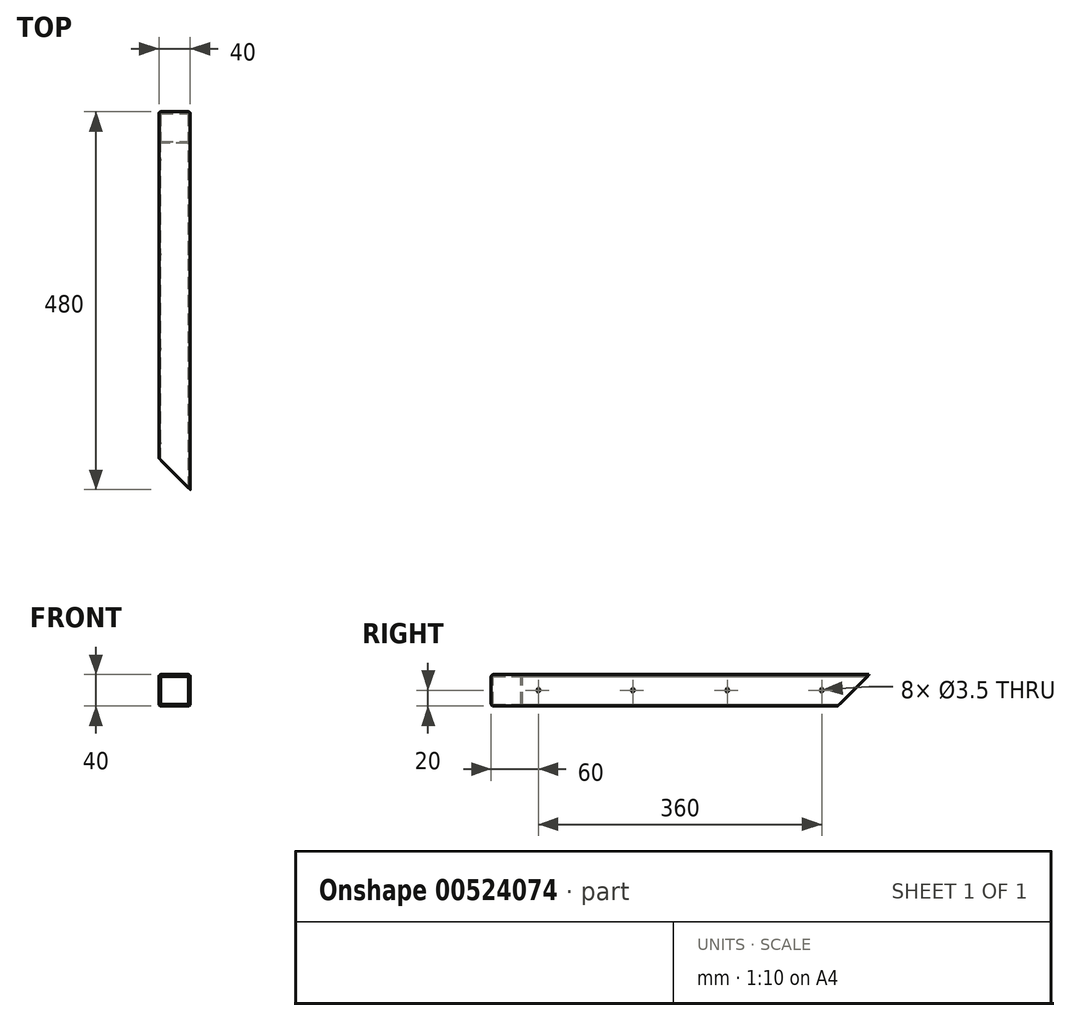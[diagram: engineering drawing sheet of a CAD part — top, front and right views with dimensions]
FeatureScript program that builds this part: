
annotation { "Feature Type Name" : "Feature", "Feature Type Description" : "" }
export const myFeature = defineFeature(function(context is Context, id is Id, definition is map)
    precondition{}
    {
        {
            assignVariable(context, id + "F0", {"name" : "R", "anyValue" : 3});
        }
        {
            assignVariable(context, id + "F1", {"name" : "W", "anyValue" : 2});
        }
        {
            var Q0;
            Q0=qCreatedBy(makeId("Front.planeOp"),FACE);
            var sketch = newSketch(context, id + "F2", { "sketchPlane" : qUnion([Q0])});
            skLineSegment(sketch, "E0.bottom", {"start": v(-20, 20) * mm, "end": v(20, 20) * mm});
            skLineSegment(sketch, "E0.top", {"start": v(-20, -20) * mm, "end": v(20, -20) * mm});
            skLineSegment(sketch, "E0.left", {"start": v(-20, 20) * mm, "end": v(-20, -20) * mm});
            skLineSegment(sketch, "E0.right", {"start": v(20, 20) * mm, "end": v(20, -20) * mm});
            skSolve(sketch);
        }
        {
            var Q0;
            Q0=qSketchRegion(id+"F2",true);
            extrude(context, id + "F3", {"entities" : qUnion([Q0]), "endBound" : BoundingType.SYMMETRIC, "depth" : 480 * mm, "offsetDistance" : 25 * mm});
        }
        {
            var Q0;
            Q0=makeQuery(id+"F3.opExtrude","SWEPT_EDGE",EDGE,{"disambiguationData":[OSD([sQuery(id+"F2.wireOp",EDGE,"E0.bottom"),sQuery(id+"F2.wireOp",EDGE,"E0.right")])]});
            var Q1;
            Q1=makeQuery(id+"F3.opExtrude","SWEPT_EDGE",EDGE,{"disambiguationData":[OSD([sQuery(id+"F2.wireOp",EDGE,"E0.bottom"),sQuery(id+"F2.wireOp",EDGE,"E0.left")])]});
            var Q2;
            Q2=makeQuery(id+"F3.opExtrude","SWEPT_EDGE",EDGE,{"disambiguationData":[OSD([sQuery(id+"F2.wireOp",EDGE,"E0.top"),sQuery(id+"F2.wireOp",EDGE,"E0.right")])]});
            var Q3;
            Q3=makeQuery(id+"F3.opExtrude","SWEPT_EDGE",EDGE,{"disambiguationData":[OSD([sQuery(id+"F2.wireOp",EDGE,"E0.top"),sQuery(id+"F2.wireOp",EDGE,"E0.left")])]});
            fillet(context, id + "F4", {"entities" : qUnion([Q0, Q1, Q2, Q3]), "radius" : (getVariable(context, 'R')) * mm, "tangentPropagation" : true, "allowEdgeOverflow" : false});
        }
        {
            var Q0;
            Q0=makeQuery(id+"F3.opExtrude","CAP_FACE",FACE,{"disambiguationData":[OSD([sQuery(id+"F2.wireOp",EDGE,"E0.bottom"),sQuery(id+"F2.wireOp",EDGE,"E0.top"),sQuery(id+"F2.wireOp",EDGE,"E0.left"),sQuery(id+"F2.wireOp",EDGE,"E0.right")])],"isStart":false});
            var Q1;
            Q1=makeQuery(id+"F3.opExtrude","CAP_FACE",FACE,{"disambiguationData":[OSD([sQuery(id+"F2.wireOp",EDGE,"E0.bottom"),sQuery(id+"F2.wireOp",EDGE,"E0.top"),sQuery(id+"F2.wireOp",EDGE,"E0.left"),sQuery(id+"F2.wireOp",EDGE,"E0.right")])],"isStart":true});
            shell(context, id + "F5", {"entities" : qUnion([Q0, Q1]), "thickness" : (getVariable(context, 'W')) * mm});
        }
        {
            var Q0;
            Q0=makeQuery(id+"F3.opExtrude","SWEPT_FACE",FACE,{"disambiguationData":[OSD([sQuery(id+"F2.wireOp",EDGE,"E0.left")])]});
            var sketch = newSketch(context, id + "F6", { "sketchPlane" : qUnion([Q0])});
            skLineSegment(sketch, "E1", {"start": v(-240, -20) * mm, "end": v(-200, -20) * mm});
            skLineSegment(sketch, "E2", {"start": v(-200, -20) * mm, "end": v(-240, 20) * mm});
            skLineSegment(sketch, "E3", {"start": v(-240, 20) * mm, "end": v(-240, -20) * mm});
            skSolve(sketch);
        }
        {
            var Q0;
            Q0=qSketchRegion(id+"F6",true);
            extrude(context, id + "F7", {"entities" : qUnion([Q0]), "operationType" : NewBodyOperationType.REMOVE, "endBound" : BoundingType.THROUGH_ALL, "oppositeDirection" : true, "depth" : 25 * mm, "offsetDistance" : 25 * mm});
        }
        {
            var Q0;
            Q0=makeQuery(id+"F3.opExtrude","SWEPT_FACE",FACE,{"disambiguationData":[OSD([sQuery(id+"F2.wireOp",EDGE,"E0.bottom")])]});
            var sketch = newSketch(context, id + "F8", { "sketchPlane" : qUnion([Q0])});
            skLineSegment(sketch, "E4.0", {"start": v(20, 237) * mm, "end": v(20, -240) * mm, "construction": true});
            skLineSegment(sketch, "E5", {"start": v(-20, -240) * mm, "end": v(20, -240) * mm});
            skLineSegment(sketch, "E6", {"start": v(20, -155) * mm, "end": v(20, -240) * mm});
            skLineSegment(sketch, "E7.0", {"start": v(-20, -240) * mm, "end": v(-20, 237) * mm, "construction": true});
            skLineSegment(sketch, "E8", {"start": v(20, -240) * mm, "end": v(-20, -200) * mm});
            skLineSegment(sketch, "E9", {"start": v(-20, -200) * mm, "end": v(-20, -240) * mm});
            skSolve(sketch);
        }
        {
            var Q0;
            Q0=qSketchRegion(id+"F8",true);
            extrude(context, id + "F9", {"entities" : qUnion([Q0]), "operationType" : NewBodyOperationType.REMOVE, "endBound" : BoundingType.THROUGH_ALL, "oppositeDirection" : true, "depth" : 25 * mm, "offsetDistance" : 25 * mm});
        }
        {
            var Q0;
            Q0=makeQuery(id+"F3.opExtrude","SWEPT_FACE",FACE,{"disambiguationData":[OSD([sQuery(id+"F2.wireOp",EDGE,"E0.left")])]});
            var sketch = newSketch(context, id + "F10", { "sketchPlane" : qUnion([Q0])});
            skPoint(sketch, "E10", {"position": v(-180, 0) * mm});
            skPoint(sketch, "E11", {"position": v(-60, 0) * mm});
            skPoint(sketch, "E12", {"position": v(60, 0) * mm});
            skPoint(sketch, "E13", {"position": v(180, 0) * mm});
            skSolve(sketch);
        }
        {
            var Q0;
            Q0=sQuery(id+"F10.wireOp",VERTEX,"E10");
            var Q1;
            Q1=sQuery(id+"F10.wireOp",VERTEX,"E11");
            var Q2;
            Q2=sQuery(id+"F10.wireOp",VERTEX,"E12");
            var Q3;
            Q3=sQuery(id+"F10.wireOp",VERTEX,"E13");
            var Q4;
            Q4=makeQuery(id+"F3.opExtrude","SWEPT_BODY",BODY,{"disambiguationData":[OSD([sQuery(id+"F2.wireOp",EDGE,"E0.bottom"),sQuery(id+"F2.wireOp",EDGE,"E0.top"),sQuery(id+"F2.wireOp",EDGE,"E0.left"),sQuery(id+"F2.wireOp",EDGE,"E0.right")])]});
            hole(context, id + "F11", {"style" : HoleStyle.C_SINK, "endStyle" : HoleEndStyle.THROUGH, "holeDiameter" : 3.5 * mm, "cSinkDiameter" : 6 * mm, "cSinkAngle" : 90 * degree, "isTappedThrough" : true, "tappedDepth" : 12 * mm, "tapClearance" : 3, "locations" : qUnion([Q0, Q1, Q2, Q3]), "scope" : qUnion([Q4])});
        }
    });
